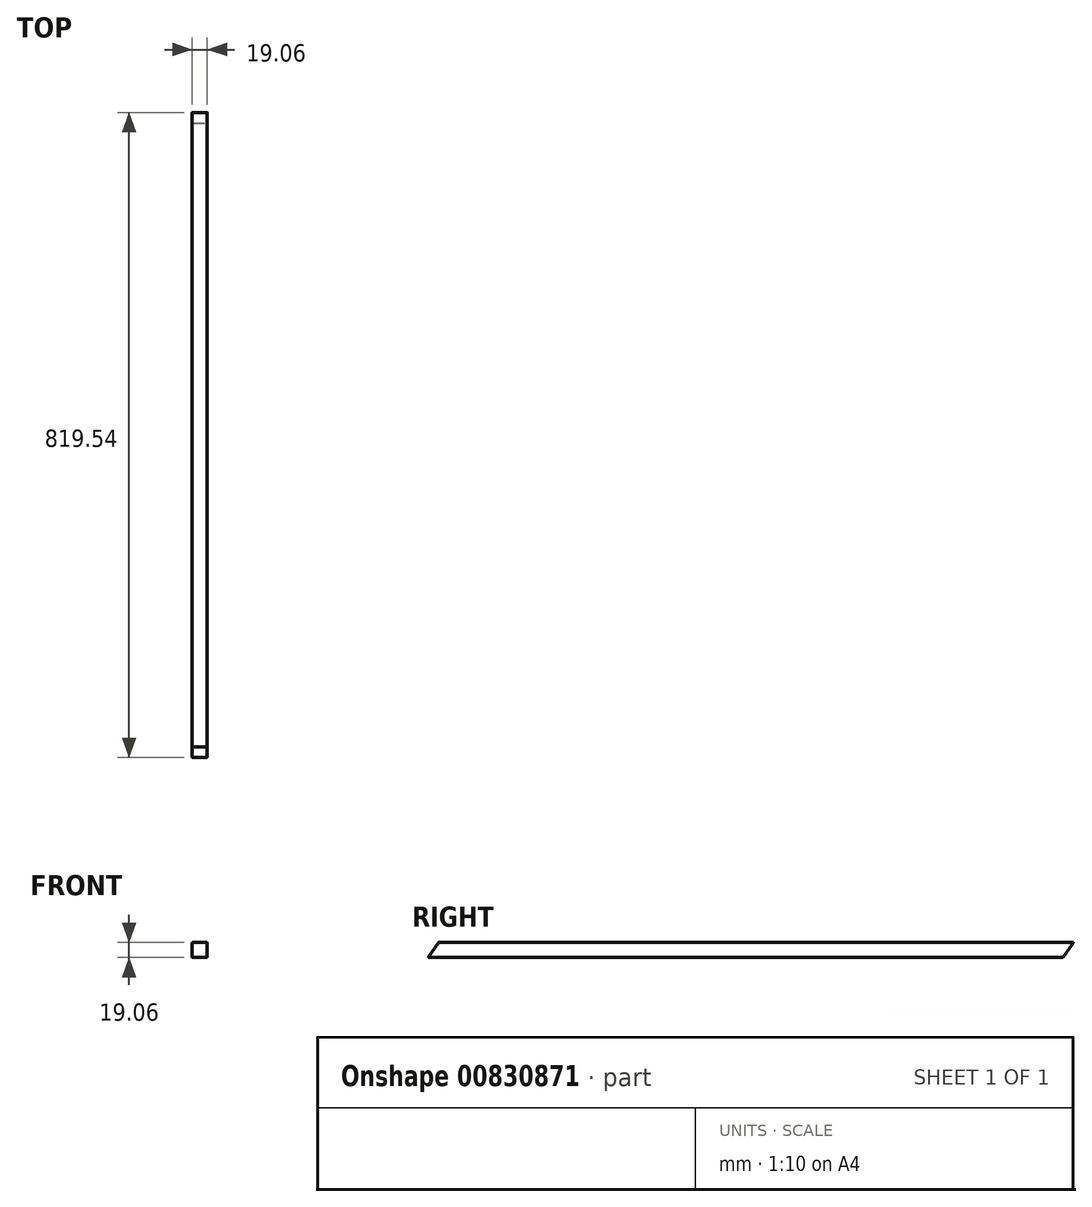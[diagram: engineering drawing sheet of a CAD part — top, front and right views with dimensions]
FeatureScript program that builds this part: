
annotation { "Feature Type Name" : "Feature", "Feature Type Description" : "" }
export const myFeature = defineFeature(function(context is Context, id is Id, definition is map)
    precondition{}
    {
        {
            var Q0;
            Q0=qCreatedBy(makeId("Front.planeOp"),FACE);
            var sketch = newSketch(context, id + "F0", { "sketchPlane" : qUnion([Q0])});
            skLineSegment(sketch, "E0.bottom", {"start": v(-8.76, 9.53) * mm, "end": v(8.76, 9.53) * mm});
            skLineSegment(sketch, "E0.top", {"start": v(-8.76, -9.53) * mm, "end": v(8.76, -9.53) * mm});
            skLineSegment(sketch, "E0.left", {"start": v(-9.53, 8.76) * mm, "end": v(-9.53, -8.76) * mm});
            skLineSegment(sketch, "E0.right", {"start": v(9.53, 8.76) * mm, "end": v(9.53, -8.76) * mm});
            skPoint(sketch, "E0.middle", {"position": v(0, 0) * mm});
            skPoint(sketch, "E1.visualSharp", {"position": v(-9.52, 9.53) * mm});
            skArc(sketch, "E1.filletArc", {"start": v(-8.76, 9.53) * mm, "mid": v(-9.3, 9.3) * mm, "end": v(-9.53, 8.76) * mm});
            skPoint(sketch, "E2.visualSharp", {"position": v(9.53, 9.53) * mm});
            skArc(sketch, "E2.filletArc", {"start": v(9.53, 8.76) * mm, "mid": v(9.3, 9.3) * mm, "end": v(8.76, 9.53) * mm});
            skPoint(sketch, "E3.visualSharp", {"position": v(9.53, -9.53) * mm});
            skArc(sketch, "E3.filletArc", {"start": v(8.76, -9.53) * mm, "mid": v(9.3, -9.3) * mm, "end": v(9.53, -8.76) * mm});
            skPoint(sketch, "E4.visualSharp", {"position": v(-9.53, -9.53) * mm});
            skArc(sketch, "E4.filletArc", {"start": v(-9.53, -8.76) * mm, "mid": v(-9.3, -9.3) * mm, "end": v(-8.76, -9.53) * mm});
            skSolve(sketch);
        }
        {
            var Q0;
            Q0 = qSketchRegion(id + "F0", true);
            extrude(context, id + "F1", {"entities" : qUnion([Q0]), "endBound" : BoundingType.SYMMETRIC, "depth" : 1016 * mm, "offsetDistance" : 25.4 * mm});
        }
        {
            var Q0;
            Q0=qCreatedBy(makeId("Right.planeOp"),FACE);
            var sketch = newSketch(context, id + "F2", { "sketchPlane" : qUnion([Q0])});
            skLineSegment(sketch, "E5", {"start": v(-508, -9.53) * mm, "end": v(-508, 24.22) * mm});
            skLineSegment(sketch, "E6", {"start": v(-508, 24.22) * mm, "end": v(-484.37, 24.22) * mm});
            skLineSegment(sketch, "E7", {"start": v(-484.37, 24.22) * mm, "end": v(-508, -9.53) * mm});
            skLineSegment(sketch, "E8", {"start": v(508, 290.1) * mm, "end": v(298.2, -9.53) * mm});
            skLineSegment(sketch, "E9", {"start": v(298.2, -9.53) * mm, "end": v(508, -9.53) * mm});
            skLineSegment(sketch, "E10", {"start": v(508, -9.52) * mm, "end": v(508, 290.1) * mm});
            skSolve(sketch);
        }
        {
            var Q0;
            Q0 = qSketchRegion(id + "F2", true);
            extrude(context, id + "F3", {"entities" : qUnion([Q0]), "operationType" : NewBodyOperationType.REMOVE, "endBound" : BoundingType.SYMMETRIC, "oppositeDirection" : true, "depth" : 50.8 * mm, "offsetDistance" : 25.4 * mm});
        }
    });
